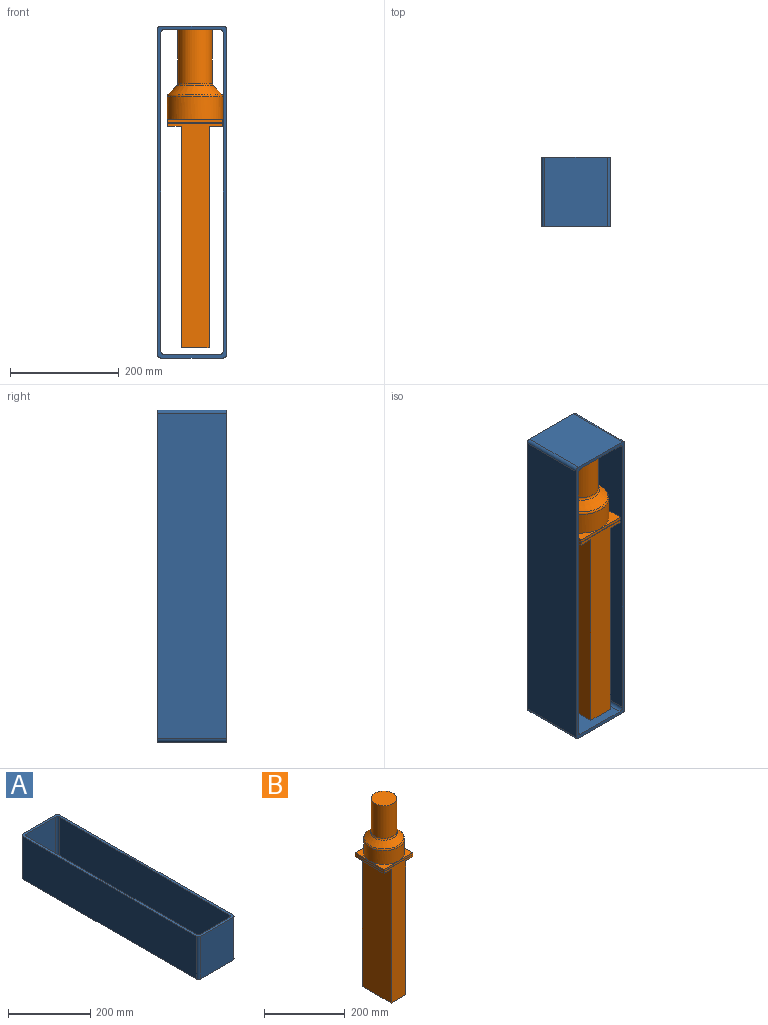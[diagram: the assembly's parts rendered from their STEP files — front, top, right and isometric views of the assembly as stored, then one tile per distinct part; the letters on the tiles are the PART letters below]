
ASSEMBLY  parts=2 mates=1
PART A: 18 faces, bbox 127x609.6x127 mm
  f0: plane 127x114.3mm, normal (0,1,0), area 14516.1mm2, adj f8,f9,f14,f17
  f1: plane 596.9x127mm, normal (-1,0,0), area 75806.3mm2, adj f8,f9,f14,f15
  f2: plane 127x114.3mm, normal (0,-1,0), area 14516.1mm2, adj f8,f9,f15,f16
  f3: plane 584.2x127mm, normal (1,0,0), area 74193.4mm2, adj f8,f9,f10,f13
  f4: plane 127x101.6mm, normal (0,-1,0), area 12903.2mm2, adj f8,f9,f10,f11
  f5: plane 584.2x127mm, normal (-1,0,0), area 74193.4mm2, adj f8,f9,f11,f12
  f6: plane 127x101.6mm, normal (0,1,0), area 12903.2mm2, adj f8,f9,f12,f13
  f7: plane 596.9x127mm, normal (1,0,0), area 75806.3mm2, adj f8,f9,f16,f17
  f8: plane 609.6x127mm, normal (0,0,1), area 9193.5mm2, adj f0,f1,f2,f3,f4,f5,f6,f7
  f9: plane 609.6x127mm, normal (0,0,-1), area 9193.5mm2, adj f0,f1,f2,f3,f4,f5,f6,f7
  f10: cylinder r=6.35mm len=127mm, axis (0,0,-1), area 1266.8mm2, adj f3,f4,f8,f9
  f11: cylinder r=6.35mm len=127mm, axis (0,0,1), area 1266.8mm2, adj f4,f5,f8,f9
  f12: cylinder r=6.35mm len=127mm, axis (0,0,-1), area 1266.8mm2, adj f5,f6,f8,f9
  f13: cylinder r=6.35mm len=127mm, axis (0,0,1), area 1266.8mm2, adj f3,f6,f8,f9
  f14: cylinder r=6.35mm len=127mm, axis (0,0,1), area 1266.8mm2, adj f0,f1,f8,f9
  f15: cylinder r=6.35mm len=127mm, axis (0,0,-1), area 1266.8mm2, adj f1,f2,f8,f9
  f16: cylinder r=6.35mm len=127mm, axis (0,0,1), area 1266.8mm2, adj f2,f7,f8,f9
  f17: cylinder r=6.35mm len=127mm, axis (0,0,-1), area 1266.8mm2, adj f0,f7,f8,f9
PART B: 28 faces, bbox 110x110x584.2 mm
  f0: plane 50.67x47.21mm, normal (0,0,1), area 547.7mm2, adj f17,f18,f22
  f1: plane 50.67x47.21mm, normal (0,0,1), area 547.7mm2, adj f18,f19,f22
  f2: plane 101.6x50.93mm, normal (0,0,1), area 1120.5mm2, adj f17,f19,f20,f22
  f3: plane 406.4x101.6mm, normal (-1,0,0), area 41290.2mm2, adj f5,f6,f7,f11
  f4: plane 406.4x101.6mm, normal (1,0,0), area 41290.2mm2, adj f5,f6,f7,f8
  f5: plane 101.6x50.8mm, normal (0,0,-1), area 5161.3mm2, adj f3,f4,f6,f7
  f6: plane 412.5x101.6mm, normal (0,1,0), area 21264.5mm2, adj f3,f4,f5,f8,f9,f10,f11,f14
  f7: plane 412.5x101.6mm, normal (0,-1,0), area 21264.5mm2, adj f3,f4,f5,f8,f9,f10,f11,f13
  f8: plane 101.6x25.4mm, normal (0,0,-1), area 2580.6mm2, adj f4,f6,f7,f9
  f9: plane 101.6x6.1mm, normal (1,0,0), area 619.4mm2, adj f6,f7,f8,f15
  f10: plane 101.6x6.1mm, normal (-1,0,0), area 619.4mm2, adj f6,f7,f11,f12
  f11: plane 101.6x25.4mm, normal (0,0,-1), area 2580.6mm2, adj f3,f6,f7,f10
  f12: cylinder r=0.25mm len=101.6mm, axis (0,-1,0), area 40.5mm2, adj f10,f13,f14,f16
  f13: cylinder r=0.25mm len=101.6mm, axis (1,0,0), area 40.5mm2, adj f7,f12,f15,f16
  f14: cylinder r=0.25mm len=101.6mm, axis (1,0,0), area 40.5mm2, adj f6,f12,f15,f18
  f15: cylinder r=0.25mm len=101.6mm, axis (0,1,0), area 40.5mm2, adj f9,f13,f14,f17
  f16: plane 101.6x101.6mm, normal (0,0,-1), area 103mm2, adj f12,f13,f17,f18,f19,f20
  f17: plane 101.6x6.35mm, normal (1,0,0), area 645.2mm2, adj f0,f2,f15,f16,f18,f20
  f18: plane 101.6x6.35mm, normal (0,1,0), area 645.2mm2, adj f0,f1,f14,f16,f17,f19,f21
  f19: plane 101.6x6.35mm, normal (-1,0,0), area 645.2mm2, adj f1,f2,f16,f18,f20
  f20: plane 101.6x6.35mm, normal (0,-1,0), area 645.2mm2, adj f2,f16,f17,f19
  f21: plane 7.18x0.13mm, normal (0,0,-1), area 0.6mm2, adj f18,f22
  f22: cylinder r=50.8mm len=101.6mm, axis (0,0,-1), area 13348.3mm2, adj f0,f1,f2,f21,f27
  f23: cone r=31.75mm half-angle=45deg, axis (0,0,-1), area 5622.5mm2, adj f26,f27
  f24: cylinder r=31.75mm len=98.97mm, axis (0,0,-1), area 19743.6mm2, adj f25,f26
  f25: plane 63.5x63.5mm, normal (0,0,1), area 3166.9mm2, adj f24
  f26: torus R=38.1mm, axis (0,0,1), area 1014.8mm2, adj f23,f24
  f27: torus R=44.45mm, axis (0,0,1), area 1572mm2, adj f22,f23
PLACE A rot(axis=(1,0,0),90deg) t=(-102.93,145.11,196.32)mm
PLACE B t=(-111.58,23.51,-27.63)mm
MATE parallel A.f4 <-> B.f22  axis (0,0,-1) through (-109.9,81.61,493.62)mm
